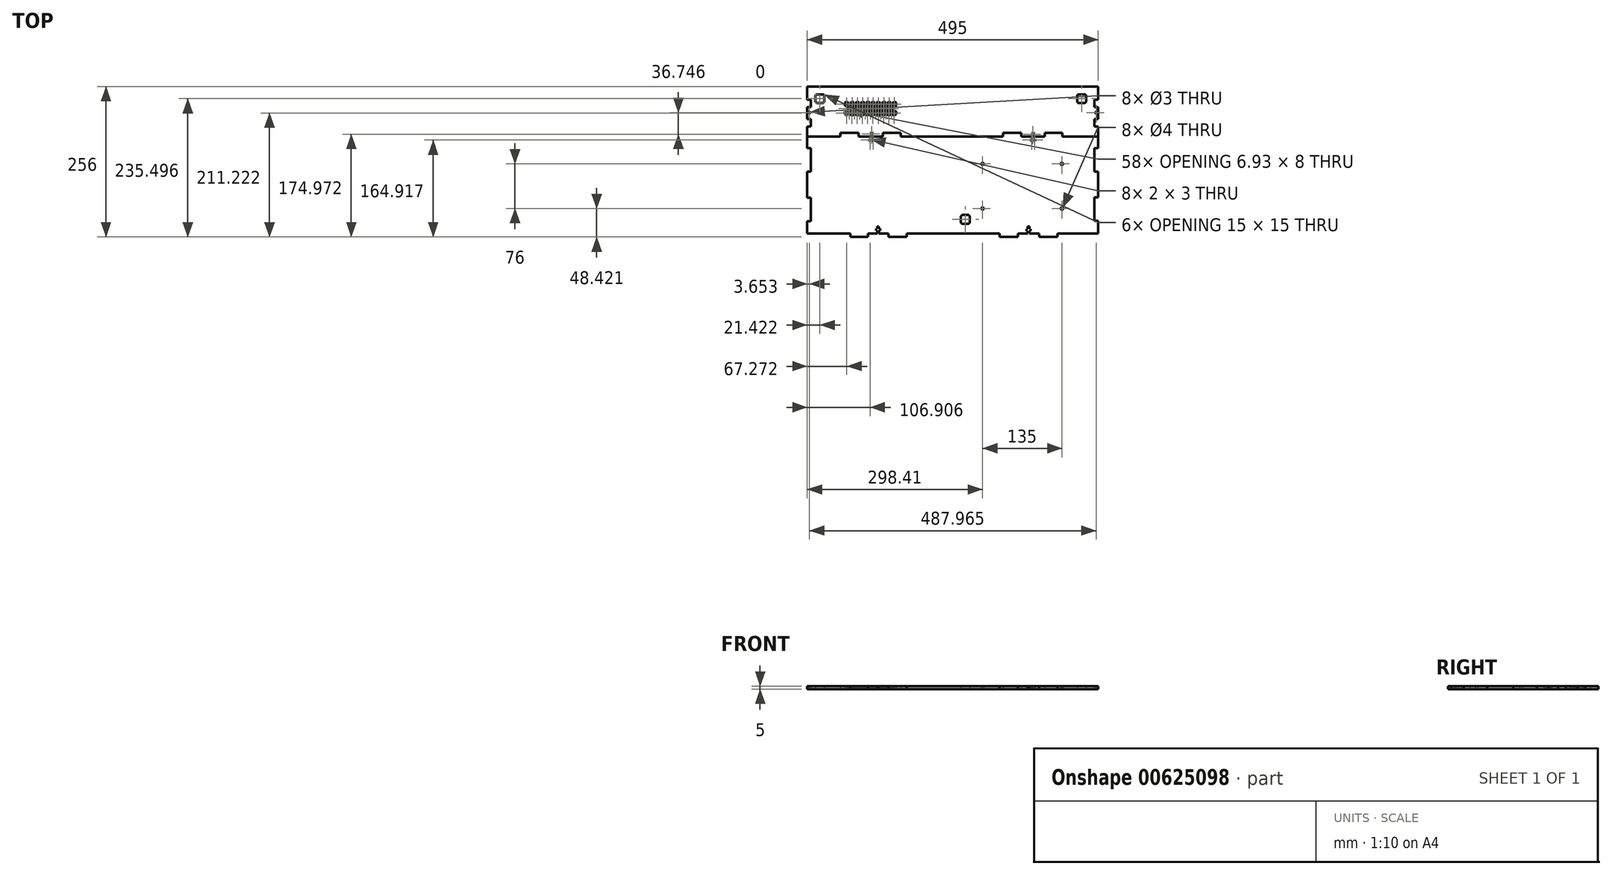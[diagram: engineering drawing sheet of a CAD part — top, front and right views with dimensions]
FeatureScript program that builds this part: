
annotation { "Feature Type Name" : "Feature", "Feature Type Description" : "" }
export const myFeature = defineFeature(function(context is Context, id is Id, definition is map)
    precondition{}
    {
        {
            var Q0;
            Q0=qCreatedBy(makeId("Top.planeOp"),FACE);
            var sketch = newSketch(context, id + "F0", { "sketchPlane" : qUnion([Q0])});
            skLineSegment(sketch, "E0", {"start": v(-326.42, 225.57) * mm, "end": v(-326.42, -168.8) * mm, "construction": true});
            skLineSegment(sketch, "E1", {"start": v(373.58, 224.27) * mm, "end": v(373.58, -247.98) * mm, "construction": true});
            skLineSegment(sketch, "E2.bottom", {"start": v(-274, -72) * mm, "end": v(221, -72) * mm});
            skLineSegment(sketch, "E2.top", {"start": v(-274, -237) * mm, "end": v(221, -237) * mm});
            skLineSegment(sketch, "E2.left", {"start": v(-274, -72) * mm, "end": v(-274, -237) * mm});
            skLineSegment(sketch, "E2.right", {"start": v(221, -72) * mm, "end": v(221, -237) * mm});
            skLineSegment(sketch, "E3", {"start": v(-200.57, -237) * mm, "end": v(-200.57, -243) * mm});
            skLineSegment(sketch, "E4", {"start": v(-200.57, -243) * mm, "end": v(-170.57, -243) * mm});
            skLineSegment(sketch, "E5", {"start": v(-170.57, -243) * mm, "end": v(-170.57, -237) * mm});
            skLineSegment(sketch, "E6", {"start": v(-135.94, -237) * mm, "end": v(-135.94, -243) * mm});
            skLineSegment(sketch, "E7", {"start": v(-135.94, -243) * mm, "end": v(-104.94, -243) * mm});
            skLineSegment(sketch, "E8", {"start": v(-104.94, -243) * mm, "end": v(-104.94, -237) * mm});
            skLineSegment(sketch, "E9", {"start": v(-186.48, -72) * mm, "end": v(-186.48, -66) * mm});
            skLineSegment(sketch, "E10", {"start": v(-186.48, -66) * mm, "end": v(-217.48, -66) * mm});
            skLineSegment(sketch, "E11", {"start": v(-217.48, -66) * mm, "end": v(-217.48, -72) * mm});
            skLineSegment(sketch, "E12", {"start": v(-114.63, -72) * mm, "end": v(-114.63, -66) * mm});
            skLineSegment(sketch, "E13", {"start": v(-114.63, -66) * mm, "end": v(-145.63, -66) * mm});
            skLineSegment(sketch, "E14", {"start": v(-145.63, -66) * mm, "end": v(-145.63, -72) * mm});
            skLineSegment(sketch, "E15", {"start": v(90.27, -72) * mm, "end": v(90.27, -66) * mm});
            skLineSegment(sketch, "E16", {"start": v(90.27, -66) * mm, "end": v(59.27, -66) * mm});
            skLineSegment(sketch, "E17", {"start": v(59.27, -66) * mm, "end": v(59.27, -72) * mm});
            skLineSegment(sketch, "E18", {"start": v(130.37, -72) * mm, "end": v(130.37, -66) * mm});
            skLineSegment(sketch, "E19", {"start": v(130.37, -66) * mm, "end": v(160.37, -66) * mm});
            skLineSegment(sketch, "E20", {"start": v(160.37, -66) * mm, "end": v(160.37, -72) * mm});
            skLineSegment(sketch, "E21", {"start": v(221, -91.47) * mm, "end": v(215, -91.47) * mm});
            skLineSegment(sketch, "E22", {"start": v(215, -91.47) * mm, "end": v(215, -131.47) * mm});
            skLineSegment(sketch, "E23", {"start": v(215, -131.47) * mm, "end": v(221, -131.47) * mm});
            skLineSegment(sketch, "E24", {"start": v(221, -175.85) * mm, "end": v(215, -175.85) * mm});
            skLineSegment(sketch, "E25", {"start": v(215, -175.85) * mm, "end": v(215, -215.85) * mm});
            skLineSegment(sketch, "E26", {"start": v(215, -215.85) * mm, "end": v(221, -215.85) * mm});
            skLineSegment(sketch, "E27", {"start": v(151.6, -237) * mm, "end": v(151.6, -243) * mm});
            skLineSegment(sketch, "E28", {"start": v(151.6, -243) * mm, "end": v(120.6, -243) * mm});
            skLineSegment(sketch, "E29", {"start": v(120.6, -243) * mm, "end": v(120.6, -237) * mm});
            skLineSegment(sketch, "E30", {"start": v(84.66, -237) * mm, "end": v(84.66, -243) * mm});
            skLineSegment(sketch, "E31", {"start": v(84.66, -243) * mm, "end": v(53.66, -243) * mm});
            skLineSegment(sketch, "E32", {"start": v(53.66, -243) * mm, "end": v(53.66, -237) * mm});
            skLineSegment(sketch, "E33", {"start": v(-274, -91.57) * mm, "end": v(-268, -91.57) * mm});
            skLineSegment(sketch, "E34", {"start": v(-268, -91.57) * mm, "end": v(-268, -131.57) * mm});
            skLineSegment(sketch, "E35", {"start": v(-268, -131.57) * mm, "end": v(-274, -131.57) * mm});
            skLineSegment(sketch, "E36", {"start": v(-274, -176.4) * mm, "end": v(-268, -176.4) * mm});
            skLineSegment(sketch, "E37", {"start": v(-268, -176.4) * mm, "end": v(-268, -216.4) * mm});
            skLineSegment(sketch, "E38", {"start": v(-268, -216.4) * mm, "end": v(-274, -216.4) * mm});
            skLineSegment(sketch, "E39", {"start": v(-155.1, -237) * mm, "end": v(-155.1, -225) * mm});
            skLineSegment(sketch, "E40", {"start": v(-155.1, -225) * mm, "end": v(-152.1, -225) * mm});
            skLineSegment(sketch, "E41", {"start": v(-152.1, -225) * mm, "end": v(-152.1, -237) * mm});
            skLineSegment(sketch, "E42", {"start": v(-155.1, -229) * mm, "end": v(-157.1, -229) * mm});
            skLineSegment(sketch, "E43", {"start": v(-157.1, -229) * mm, "end": v(-157.1, -232) * mm});
            skLineSegment(sketch, "E44", {"start": v(-157.1, -232) * mm, "end": v(-155.1, -232) * mm});
            skLineSegment(sketch, "E45", {"start": v(-152.1, -229) * mm, "end": v(-150.1, -229) * mm});
            skLineSegment(sketch, "E46", {"start": v(-150.1, -229) * mm, "end": v(-150.1, -232) * mm});
            skLineSegment(sketch, "E47", {"start": v(-150.1, -232) * mm, "end": v(-152.1, -232) * mm});
            skLineSegment(sketch, "E48", {"start": v(-308.95, -154.5) * mm, "end": v(259.37, -154.5) * mm, "construction": true});
            skLineSegment(sketch, "E49", {"start": v(-155.1, -237) * mm, "end": v(-152.1, -237) * mm});
            skLineSegment(sketch, "E50.1.0.0", {"start": v(100.9, -237) * mm, "end": v(103.9, -237) * mm});
            skLineSegment(sketch, "E50.1.0.1", {"start": v(100.9, -237) * mm, "end": v(100.9, -225) * mm});
            skLineSegment(sketch, "E50.1.0.2", {"start": v(98.9, -232.57) * mm, "end": v(100.9, -232.57) * mm});
            skLineSegment(sketch, "E50.1.0.3", {"start": v(98.9, -229.57) * mm, "end": v(98.9, -232.57) * mm});
            skLineSegment(sketch, "E50.1.0.4", {"start": v(100.9, -229.57) * mm, "end": v(98.9, -229.57) * mm});
            skLineSegment(sketch, "E50.1.0.5", {"start": v(100.9, -225) * mm, "end": v(103.9, -225) * mm});
            skLineSegment(sketch, "E50.1.0.6", {"start": v(103.9, -225) * mm, "end": v(103.9, -237) * mm});
            skLineSegment(sketch, "E50.1.0.7", {"start": v(103.9, -229.57) * mm, "end": v(105.9, -229.57) * mm});
            skLineSegment(sketch, "E50.1.0.8", {"start": v(105.9, -232.57) * mm, "end": v(103.9, -232.57) * mm});
            skLineSegment(sketch, "E50.1.0.9", {"start": v(105.9, -229.57) * mm, "end": v(105.9, -232.57) * mm});
            skLineSegment(sketch, "E50.direction1", {"start": v(-155.1, -237) * mm, "end": v(100.9, -237) * mm, "construction": true});
            skLineSegment(sketch, "E51.MirrorCS", {"start": v(108.9, -84.07) * mm, "end": v(111.9, -84.07) * mm});
            skLineSegment(sketch, "E52.MirrorCS", {"start": v(111.9, -79.57) * mm, "end": v(113.9, -79.57) * mm});
            skLineSegment(sketch, "E53.MirrorCS", {"start": v(113.9, -79.57) * mm, "end": v(113.9, -76.57) * mm});
            skLineSegment(sketch, "E54.MirrorCS", {"start": v(113.9, -76.57) * mm, "end": v(111.9, -76.57) * mm});
            skLineSegment(sketch, "E55.MirrorCS", {"start": v(111.9, -84.07) * mm, "end": v(111.9, -72.07) * mm});
            skLineSegment(sketch, "E56.MirrorCS", {"start": v(108.9, -79.57) * mm, "end": v(106.9, -79.57) * mm});
            skLineSegment(sketch, "E57.MirrorCS", {"start": v(106.9, -79.57) * mm, "end": v(106.9, -76.57) * mm});
            skLineSegment(sketch, "E58.MirrorCS", {"start": v(106.9, -76.57) * mm, "end": v(108.9, -76.57) * mm});
            skLineSegment(sketch, "E59.MirrorCS", {"start": v(108.9, -72.07) * mm, "end": v(108.9, -84.07) * mm});
            skLineSegment(sketch, "E60.MirrorCS", {"start": v(-166.1, -84.07) * mm, "end": v(-163.1, -84.07) * mm});
            skLineSegment(sketch, "E61.MirrorCS", {"start": v(-161.1, -79.57) * mm, "end": v(-161.1, -76.57) * mm});
            skLineSegment(sketch, "E62.MirrorCS", {"start": v(-163.1, -79.57) * mm, "end": v(-161.1, -79.57) * mm});
            skLineSegment(sketch, "E63.MirrorCS", {"start": v(-163.1, -84.07) * mm, "end": v(-163.1, -72.07) * mm});
            skLineSegment(sketch, "E64.MirrorCS", {"start": v(-161.1, -76.57) * mm, "end": v(-163.1, -76.57) * mm});
            skLineSegment(sketch, "E65.MirrorCS", {"start": v(-168.1, -76.57) * mm, "end": v(-166.1, -76.57) * mm});
            skLineSegment(sketch, "E66.MirrorCS", {"start": v(-168.1, -79.57) * mm, "end": v(-168.1, -76.57) * mm});
            skLineSegment(sketch, "E67.MirrorCS", {"start": v(-166.1, -72.07) * mm, "end": v(-166.1, -84.07) * mm});
            skLineSegment(sketch, "E68.MirrorCS", {"start": v(-166.1, -79.57) * mm, "end": v(-168.1, -79.57) * mm});
            skLineSegment(sketch, "E69.MirrorCS", {"start": v(100.9, -237.07) * mm, "end": v(100.9, -225.07) * mm});
            skLineSegment(sketch, "E70.bottom", {"start": v(-9.44, -205.6) * mm, "end": v(-0.44, -205.6) * mm});
            skLineSegment(sketch, "E70.top", {"start": v(-9.44, -220.6) * mm, "end": v(-0.44, -220.6) * mm});
            skLineSegment(sketch, "E70.left", {"start": v(-12.44, -208.6) * mm, "end": v(-12.44, -217.6) * mm});
            skLineSegment(sketch, "E70.right", {"start": v(2.56, -208.6) * mm, "end": v(2.56, -217.6) * mm});
            skPoint(sketch, "E71.visualSharp", {"position": v(-12.44, -205.6) * mm});
            skArc(sketch, "E71.filletArc", {"start": v(-9.44, -205.6) * mm, "mid": v(-11.56, -206.48) * mm, "end": v(-12.44, -208.6) * mm});
            skPoint(sketch, "E72.visualSharp", {"position": v(2.56, -205.6) * mm});
            skArc(sketch, "E72.filletArc", {"start": v(2.56, -208.6) * mm, "mid": v(1.69, -206.48) * mm, "end": v(-0.44, -205.6) * mm});
            skPoint(sketch, "E73.visualSharp", {"position": v(2.56, -220.6) * mm});
            skArc(sketch, "E73.filletArc", {"start": v(-0.44, -220.6) * mm, "mid": v(1.69, -219.73) * mm, "end": v(2.56, -217.6) * mm});
            skPoint(sketch, "E74.visualSharp", {"position": v(-12.44, -220.6) * mm});
            skArc(sketch, "E74.filletArc", {"start": v(-12.44, -217.6) * mm, "mid": v(-11.56, -219.73) * mm, "end": v(-9.44, -220.6) * mm});
            skCircle(sketch, "E75", {"center": v(24.41, -194.57) * mm, "radius": 2 * mm});
            skCircle(sketch, "E76.0.1.0", {"center": v(24.41, -118.57) * mm, "radius": 2 * mm});
            skCircle(sketch, "E76.1.0.0", {"center": v(159.41, -194.57) * mm, "radius": 2 * mm});
            skCircle(sketch, "E76.1.1.0", {"center": v(159.41, -118.57) * mm, "radius": 2 * mm});
            skLineSegment(sketch, "E76.direction1", {"start": v(24.41, -194.57) * mm, "end": v(159.41, -194.57) * mm, "construction": true});
            skLineSegment(sketch, "E76.direction2", {"start": v(24.41, -194.57) * mm, "end": v(24.41, -118.57) * mm, "construction": true});
            skLineSegment(sketch, "E77", {"start": v(-274, -72) * mm, "end": v(-274, 13) * mm});
            skLineSegment(sketch, "E78", {"start": v(-274, 13) * mm, "end": v(221, 13) * mm});
            skLineSegment(sketch, "E79", {"start": v(221, 13) * mm, "end": v(221, -72) * mm});
            skLineSegment(sketch, "E80", {"start": v(-274, -9.1) * mm, "end": v(-268, -9.1) * mm});
            skLineSegment(sketch, "E81", {"start": v(-268, -9.1) * mm, "end": v(-268, -22.1) * mm});
            skLineSegment(sketch, "E82", {"start": v(-268, -22.1) * mm, "end": v(-274, -22.1) * mm});
            skLineSegment(sketch, "E83", {"start": v(-274, -42.1) * mm, "end": v(-268, -42.1) * mm});
            skLineSegment(sketch, "E84", {"start": v(-268, -42.1) * mm, "end": v(-268, -55.1) * mm});
            skLineSegment(sketch, "E85", {"start": v(-268, -55.1) * mm, "end": v(-274, -55.1) * mm});
            skLineSegment(sketch, "E86", {"start": v(221, -9.1) * mm, "end": v(215, -9.1) * mm});
            skLineSegment(sketch, "E87", {"start": v(215, -9.1) * mm, "end": v(215, -22.1) * mm});
            skLineSegment(sketch, "E88", {"start": v(215, -22.1) * mm, "end": v(221, -22.1) * mm});
            skLineSegment(sketch, "E89", {"start": v(221, -42.1) * mm, "end": v(215, -42.1) * mm});
            skLineSegment(sketch, "E90", {"start": v(215, -42.1) * mm, "end": v(215, -55.1) * mm});
            skLineSegment(sketch, "E91", {"start": v(215, -55.1) * mm, "end": v(221, -55.1) * mm});
            skCircle(sketch, "E92", {"center": v(217.62, -31.36) * mm, "radius": 1.5 * mm});
            skCircle(sketch, "E93", {"center": v(-270.35, -31.27) * mm, "radius": 1.5 * mm});
            skLineSegment(sketch, "E94.bottom", {"start": v(-257.08, 0) * mm, "end": v(-248.08, 0) * mm});
            skLineSegment(sketch, "E94.top", {"start": v(-257.08, -15) * mm, "end": v(-248.08, -15) * mm});
            skLineSegment(sketch, "E94.left", {"start": v(-260.08, -3) * mm, "end": v(-260.08, -12) * mm});
            skLineSegment(sketch, "E94.right", {"start": v(-245.08, -3) * mm, "end": v(-245.08, -12) * mm});
            skPoint(sketch, "E95.visualSharp", {"position": v(-260.08, 0) * mm});
            skArc(sketch, "E95.filletArc", {"start": v(-257.08, 0) * mm, "mid": v(-259.2, -0.87) * mm, "end": v(-260.08, -3) * mm});
            skPoint(sketch, "E96.visualSharp", {"position": v(-245.08, 0) * mm});
            skArc(sketch, "E96.filletArc", {"start": v(-245.08, -3) * mm, "mid": v(-245.96, -0.87) * mm, "end": v(-248.08, 0) * mm});
            skPoint(sketch, "E97.visualSharp", {"position": v(-260.08, -15) * mm});
            skArc(sketch, "E97.filletArc", {"start": v(-260.08, -12) * mm, "mid": v(-259.2, -14.12) * mm, "end": v(-257.08, -15) * mm});
            skPoint(sketch, "E98.visualSharp", {"position": v(-245.08, -15) * mm});
            skArc(sketch, "E98.filletArc", {"start": v(-248.08, -15) * mm, "mid": v(-245.96, -14.12) * mm, "end": v(-245.08, -12) * mm});
            skLineSegment(sketch, "E99.bottom", {"start": v(188.51, 0) * mm, "end": v(197.51, 0) * mm});
            skLineSegment(sketch, "E99.top", {"start": v(188.51, -15) * mm, "end": v(197.51, -15) * mm});
            skLineSegment(sketch, "E99.left", {"start": v(185.51, -3) * mm, "end": v(185.51, -12) * mm});
            skLineSegment(sketch, "E99.right", {"start": v(200.51, -3) * mm, "end": v(200.51, -12) * mm});
            skPoint(sketch, "E100.visualSharp", {"position": v(185.51, 0) * mm});
            skArc(sketch, "E100.filletArc", {"start": v(188.51, 0) * mm, "mid": v(186.4, -0.87) * mm, "end": v(185.51, -3) * mm});
            skPoint(sketch, "E101.visualSharp", {"position": v(200.51, 0) * mm});
            skArc(sketch, "E101.filletArc", {"start": v(200.51, -3) * mm, "mid": v(199.63, -0.87) * mm, "end": v(197.51, 0) * mm});
            skPoint(sketch, "E102.visualSharp", {"position": v(185.51, -15) * mm});
            skArc(sketch, "E102.filletArc", {"start": v(185.51, -12) * mm, "mid": v(186.4, -14.12) * mm, "end": v(188.51, -15) * mm});
            skPoint(sketch, "E103.visualSharp", {"position": v(200.51, -15) * mm});
            skArc(sketch, "E103.filletArc", {"start": v(197.51, -15) * mm, "mid": v(199.63, -14.12) * mm, "end": v(200.51, -12) * mm});
            skCircle(sketch, "E104", {"center": v(-164.6, -67.51) * mm, "radius": 1.5 * mm});
            skCircle(sketch, "E105", {"center": v(110, -68.02) * mm, "radius": 1.5 * mm});
            skCircle(sketch, "E106.cCircle", {"center": v(-206.73, -17.03) * mm, "radius": 4 * mm, "construction": true});
            skLineSegment(sketch, "E106.0", {"start": v(-203.26, -15.03) * mm, "end": v(-203.26, -19.03) * mm});
            skLineSegment(sketch, "E106.1", {"start": v(-203.26, -19.03) * mm, "end": v(-206.73, -21.03) * mm});
            skLineSegment(sketch, "E106.2", {"start": v(-206.73, -21.03) * mm, "end": v(-210.2, -19.03) * mm});
            skLineSegment(sketch, "E106.3", {"start": v(-210.2, -19.03) * mm, "end": v(-210.2, -15.03) * mm});
            skLineSegment(sketch, "E106.4", {"start": v(-210.2, -15.03) * mm, "end": v(-206.73, -13.03) * mm});
            skLineSegment(sketch, "E106.5", {"start": v(-206.73, -13.03) * mm, "end": v(-203.26, -15.03) * mm});
            skLineSegment(sketch, "E107.0.1.0", {"start": v(-205.94, -26.4) * mm, "end": v(-205.94, -22.4) * mm});
            skLineSegment(sketch, "E107.0.1.1", {"start": v(-205.94, -22.4) * mm, "end": v(-202.47, -20.4) * mm});
            skLineSegment(sketch, "E107.0.1.2", {"start": v(-202.47, -20.4) * mm, "end": v(-199, -22.4) * mm});
            skLineSegment(sketch, "E107.0.1.3", {"start": v(-199, -22.4) * mm, "end": v(-199, -26.4) * mm});
            skLineSegment(sketch, "E107.0.1.4", {"start": v(-199, -26.4) * mm, "end": v(-202.47, -28.4) * mm});
            skLineSegment(sketch, "E107.0.1.5", {"start": v(-202.47, -28.4) * mm, "end": v(-205.94, -26.4) * mm});
            skLineSegment(sketch, "E107.0.2.0", {"start": v(-201.68, -33.77) * mm, "end": v(-201.68, -29.77) * mm});
            skLineSegment(sketch, "E107.0.2.1", {"start": v(-201.68, -29.77) * mm, "end": v(-198.22, -27.77) * mm});
            skLineSegment(sketch, "E107.0.2.2", {"start": v(-198.22, -27.77) * mm, "end": v(-194.75, -29.77) * mm});
            skLineSegment(sketch, "E107.0.2.3", {"start": v(-194.75, -29.77) * mm, "end": v(-194.75, -33.77) * mm});
            skLineSegment(sketch, "E107.0.2.4", {"start": v(-194.75, -33.77) * mm, "end": v(-198.22, -35.77) * mm});
            skLineSegment(sketch, "E107.0.2.5", {"start": v(-198.22, -35.77) * mm, "end": v(-201.68, -33.77) * mm});
            skLineSegment(sketch, "E107.1.0.0", {"start": v(-201.2, -19.03) * mm, "end": v(-201.2, -15.03) * mm});
            skLineSegment(sketch, "E107.1.0.1", {"start": v(-201.2, -15.03) * mm, "end": v(-197.73, -13.03) * mm});
            skLineSegment(sketch, "E107.1.0.2", {"start": v(-197.73, -13.03) * mm, "end": v(-194.26, -15.03) * mm});
            skLineSegment(sketch, "E107.1.0.3", {"start": v(-194.26, -15.03) * mm, "end": v(-194.26, -19.03) * mm});
            skLineSegment(sketch, "E107.1.0.4", {"start": v(-194.26, -19.03) * mm, "end": v(-197.73, -21.03) * mm});
            skLineSegment(sketch, "E107.1.0.5", {"start": v(-197.73, -21.03) * mm, "end": v(-201.2, -19.03) * mm});
            skLineSegment(sketch, "E107.1.1.0", {"start": v(-196.94, -26.4) * mm, "end": v(-196.94, -22.4) * mm});
            skLineSegment(sketch, "E107.1.1.1", {"start": v(-196.94, -22.4) * mm, "end": v(-193.47, -20.4) * mm});
            skLineSegment(sketch, "E107.1.1.2", {"start": v(-193.47, -20.4) * mm, "end": v(-190, -22.4) * mm});
            skLineSegment(sketch, "E107.1.1.3", {"start": v(-190, -22.4) * mm, "end": v(-190, -26.4) * mm});
            skLineSegment(sketch, "E107.1.1.4", {"start": v(-190, -26.4) * mm, "end": v(-193.47, -28.4) * mm});
            skLineSegment(sketch, "E107.1.1.5", {"start": v(-193.47, -28.4) * mm, "end": v(-196.94, -26.4) * mm});
            skLineSegment(sketch, "E107.1.2.0", {"start": v(-192.68, -33.77) * mm, "end": v(-192.68, -29.77) * mm});
            skLineSegment(sketch, "E107.1.2.1", {"start": v(-192.68, -29.77) * mm, "end": v(-189.22, -27.77) * mm});
            skLineSegment(sketch, "E107.1.2.2", {"start": v(-189.22, -27.77) * mm, "end": v(-185.75, -29.77) * mm});
            skLineSegment(sketch, "E107.1.2.3", {"start": v(-185.75, -29.77) * mm, "end": v(-185.75, -33.77) * mm});
            skLineSegment(sketch, "E107.1.2.4", {"start": v(-185.75, -33.77) * mm, "end": v(-189.22, -35.77) * mm});
            skLineSegment(sketch, "E107.1.2.5", {"start": v(-189.22, -35.77) * mm, "end": v(-192.68, -33.77) * mm});
            skLineSegment(sketch, "E107.2.0.0", {"start": v(-192.2, -19.03) * mm, "end": v(-192.2, -15.03) * mm});
            skLineSegment(sketch, "E107.2.0.1", {"start": v(-192.2, -15.03) * mm, "end": v(-188.73, -13.03) * mm});
            skLineSegment(sketch, "E107.2.0.2", {"start": v(-188.73, -13.03) * mm, "end": v(-185.26, -15.03) * mm});
            skLineSegment(sketch, "E107.2.0.3", {"start": v(-185.26, -15.03) * mm, "end": v(-185.26, -19.03) * mm});
            skLineSegment(sketch, "E107.2.0.4", {"start": v(-185.26, -19.03) * mm, "end": v(-188.73, -21.03) * mm});
            skLineSegment(sketch, "E107.2.0.5", {"start": v(-188.73, -21.03) * mm, "end": v(-192.2, -19.03) * mm});
            skLineSegment(sketch, "E107.2.1.0", {"start": v(-187.94, -26.4) * mm, "end": v(-187.94, -22.4) * mm});
            skLineSegment(sketch, "E107.2.1.1", {"start": v(-187.94, -22.4) * mm, "end": v(-184.47, -20.4) * mm});
            skLineSegment(sketch, "E107.2.1.2", {"start": v(-184.47, -20.4) * mm, "end": v(-181, -22.4) * mm});
            skLineSegment(sketch, "E107.2.1.3", {"start": v(-181, -22.4) * mm, "end": v(-181, -26.4) * mm});
            skLineSegment(sketch, "E107.2.1.4", {"start": v(-181, -26.4) * mm, "end": v(-184.47, -28.4) * mm});
            skLineSegment(sketch, "E107.2.1.5", {"start": v(-184.47, -28.4) * mm, "end": v(-187.94, -26.4) * mm});
            skLineSegment(sketch, "E107.2.2.0", {"start": v(-183.68, -33.77) * mm, "end": v(-183.68, -29.77) * mm});
            skLineSegment(sketch, "E107.2.2.1", {"start": v(-183.68, -29.77) * mm, "end": v(-180.22, -27.77) * mm});
            skLineSegment(sketch, "E107.2.2.2", {"start": v(-180.22, -27.77) * mm, "end": v(-176.75, -29.77) * mm});
            skLineSegment(sketch, "E107.2.2.3", {"start": v(-176.75, -29.77) * mm, "end": v(-176.75, -33.77) * mm});
            skLineSegment(sketch, "E107.2.2.4", {"start": v(-176.75, -33.77) * mm, "end": v(-180.22, -35.77) * mm});
            skLineSegment(sketch, "E107.2.2.5", {"start": v(-180.22, -35.77) * mm, "end": v(-183.68, -33.77) * mm});
            skLineSegment(sketch, "E107.3.0.0", {"start": v(-183.2, -19.03) * mm, "end": v(-183.2, -15.03) * mm});
            skLineSegment(sketch, "E107.3.0.1", {"start": v(-183.2, -15.03) * mm, "end": v(-179.73, -13.03) * mm});
            skLineSegment(sketch, "E107.3.0.2", {"start": v(-179.73, -13.03) * mm, "end": v(-176.26, -15.03) * mm});
            skLineSegment(sketch, "E107.3.0.3", {"start": v(-176.26, -15.03) * mm, "end": v(-176.26, -19.03) * mm});
            skLineSegment(sketch, "E107.3.0.4", {"start": v(-176.26, -19.03) * mm, "end": v(-179.73, -21.03) * mm});
            skLineSegment(sketch, "E107.3.0.5", {"start": v(-179.73, -21.03) * mm, "end": v(-183.2, -19.03) * mm});
            skLineSegment(sketch, "E107.3.1.0", {"start": v(-178.94, -26.4) * mm, "end": v(-178.94, -22.4) * mm});
            skLineSegment(sketch, "E107.3.1.1", {"start": v(-178.94, -22.4) * mm, "end": v(-175.47, -20.4) * mm});
            skLineSegment(sketch, "E107.3.1.2", {"start": v(-175.47, -20.4) * mm, "end": v(-172, -22.4) * mm});
            skLineSegment(sketch, "E107.3.1.3", {"start": v(-172, -22.4) * mm, "end": v(-172, -26.4) * mm});
            skLineSegment(sketch, "E107.3.1.4", {"start": v(-172, -26.4) * mm, "end": v(-175.47, -28.4) * mm});
            skLineSegment(sketch, "E107.3.1.5", {"start": v(-175.47, -28.4) * mm, "end": v(-178.94, -26.4) * mm});
            skLineSegment(sketch, "E107.3.2.0", {"start": v(-174.68, -33.77) * mm, "end": v(-174.68, -29.77) * mm});
            skLineSegment(sketch, "E107.3.2.1", {"start": v(-174.68, -29.77) * mm, "end": v(-171.22, -27.77) * mm});
            skLineSegment(sketch, "E107.3.2.2", {"start": v(-171.22, -27.77) * mm, "end": v(-167.75, -29.77) * mm});
            skLineSegment(sketch, "E107.3.2.3", {"start": v(-167.75, -29.77) * mm, "end": v(-167.75, -33.77) * mm});
            skLineSegment(sketch, "E107.3.2.4", {"start": v(-167.75, -33.77) * mm, "end": v(-171.22, -35.77) * mm});
            skLineSegment(sketch, "E107.3.2.5", {"start": v(-171.22, -35.77) * mm, "end": v(-174.68, -33.77) * mm});
            skLineSegment(sketch, "E107.4.0.0", {"start": v(-174.2, -19.03) * mm, "end": v(-174.2, -15.03) * mm});
            skLineSegment(sketch, "E107.4.0.1", {"start": v(-174.2, -15.03) * mm, "end": v(-170.73, -13.03) * mm});
            skLineSegment(sketch, "E107.4.0.2", {"start": v(-170.73, -13.03) * mm, "end": v(-167.26, -15.03) * mm});
            skLineSegment(sketch, "E107.4.0.3", {"start": v(-167.26, -15.03) * mm, "end": v(-167.26, -19.03) * mm});
            skLineSegment(sketch, "E107.4.0.4", {"start": v(-167.26, -19.03) * mm, "end": v(-170.73, -21.03) * mm});
            skLineSegment(sketch, "E107.4.0.5", {"start": v(-170.73, -21.03) * mm, "end": v(-174.2, -19.03) * mm});
            skLineSegment(sketch, "E107.4.1.0", {"start": v(-169.94, -26.4) * mm, "end": v(-169.94, -22.4) * mm});
            skLineSegment(sketch, "E107.4.1.1", {"start": v(-169.94, -22.4) * mm, "end": v(-166.47, -20.4) * mm});
            skLineSegment(sketch, "E107.4.1.2", {"start": v(-166.47, -20.4) * mm, "end": v(-163, -22.4) * mm});
            skLineSegment(sketch, "E107.4.1.3", {"start": v(-163, -22.4) * mm, "end": v(-163, -26.4) * mm});
            skLineSegment(sketch, "E107.4.1.4", {"start": v(-163, -26.4) * mm, "end": v(-166.47, -28.4) * mm});
            skLineSegment(sketch, "E107.4.1.5", {"start": v(-166.47, -28.4) * mm, "end": v(-169.94, -26.4) * mm});
            skLineSegment(sketch, "E107.4.2.0", {"start": v(-165.68, -33.77) * mm, "end": v(-165.68, -29.77) * mm});
            skLineSegment(sketch, "E107.4.2.1", {"start": v(-165.68, -29.77) * mm, "end": v(-162.22, -27.77) * mm});
            skLineSegment(sketch, "E107.4.2.2", {"start": v(-162.22, -27.77) * mm, "end": v(-158.75, -29.77) * mm});
            skLineSegment(sketch, "E107.4.2.3", {"start": v(-158.75, -29.77) * mm, "end": v(-158.75, -33.77) * mm});
            skLineSegment(sketch, "E107.4.2.4", {"start": v(-158.75, -33.77) * mm, "end": v(-162.22, -35.77) * mm});
            skLineSegment(sketch, "E107.4.2.5", {"start": v(-162.22, -35.77) * mm, "end": v(-165.68, -33.77) * mm});
            skLineSegment(sketch, "E107.5.0.0", {"start": v(-165.2, -19.03) * mm, "end": v(-165.2, -15.03) * mm});
            skLineSegment(sketch, "E107.5.0.1", {"start": v(-165.2, -15.03) * mm, "end": v(-161.73, -13.03) * mm});
            skLineSegment(sketch, "E107.5.0.2", {"start": v(-161.73, -13.03) * mm, "end": v(-158.26, -15.03) * mm});
            skLineSegment(sketch, "E107.5.0.3", {"start": v(-158.26, -15.03) * mm, "end": v(-158.26, -19.03) * mm});
            skLineSegment(sketch, "E107.5.0.4", {"start": v(-158.26, -19.03) * mm, "end": v(-161.73, -21.03) * mm});
            skLineSegment(sketch, "E107.5.0.5", {"start": v(-161.73, -21.03) * mm, "end": v(-165.2, -19.03) * mm});
            skLineSegment(sketch, "E107.5.1.0", {"start": v(-160.94, -26.4) * mm, "end": v(-160.94, -22.4) * mm});
            skLineSegment(sketch, "E107.5.1.1", {"start": v(-160.94, -22.4) * mm, "end": v(-157.47, -20.4) * mm});
            skLineSegment(sketch, "E107.5.1.2", {"start": v(-157.47, -20.4) * mm, "end": v(-154, -22.4) * mm});
            skLineSegment(sketch, "E107.5.1.3", {"start": v(-154, -22.4) * mm, "end": v(-154, -26.4) * mm});
            skLineSegment(sketch, "E107.5.1.4", {"start": v(-154, -26.4) * mm, "end": v(-157.47, -28.4) * mm});
            skLineSegment(sketch, "E107.5.1.5", {"start": v(-157.47, -28.4) * mm, "end": v(-160.94, -26.4) * mm});
            skLineSegment(sketch, "E107.5.2.0", {"start": v(-156.68, -33.77) * mm, "end": v(-156.68, -29.77) * mm});
            skLineSegment(sketch, "E107.5.2.1", {"start": v(-156.68, -29.77) * mm, "end": v(-153.22, -27.77) * mm});
            skLineSegment(sketch, "E107.5.2.2", {"start": v(-153.22, -27.77) * mm, "end": v(-149.75, -29.77) * mm});
            skLineSegment(sketch, "E107.5.2.3", {"start": v(-149.75, -29.77) * mm, "end": v(-149.75, -33.77) * mm});
            skLineSegment(sketch, "E107.5.2.4", {"start": v(-149.75, -33.77) * mm, "end": v(-153.22, -35.77) * mm});
            skLineSegment(sketch, "E107.5.2.5", {"start": v(-153.22, -35.77) * mm, "end": v(-156.68, -33.77) * mm});
            skLineSegment(sketch, "E107.6.0.0", {"start": v(-156.2, -19.03) * mm, "end": v(-156.2, -15.03) * mm});
            skLineSegment(sketch, "E107.6.0.1", {"start": v(-156.2, -15.03) * mm, "end": v(-152.73, -13.03) * mm});
            skLineSegment(sketch, "E107.6.0.2", {"start": v(-152.73, -13.03) * mm, "end": v(-149.26, -15.03) * mm});
            skLineSegment(sketch, "E107.6.0.3", {"start": v(-149.26, -15.03) * mm, "end": v(-149.26, -19.03) * mm});
            skLineSegment(sketch, "E107.6.0.4", {"start": v(-149.26, -19.03) * mm, "end": v(-152.73, -21.03) * mm});
            skLineSegment(sketch, "E107.6.0.5", {"start": v(-152.73, -21.03) * mm, "end": v(-156.2, -19.03) * mm});
            skLineSegment(sketch, "E107.6.1.0", {"start": v(-151.94, -26.4) * mm, "end": v(-151.94, -22.4) * mm});
            skLineSegment(sketch, "E107.6.1.1", {"start": v(-151.94, -22.4) * mm, "end": v(-148.47, -20.4) * mm});
            skLineSegment(sketch, "E107.6.1.2", {"start": v(-148.47, -20.4) * mm, "end": v(-145, -22.4) * mm});
            skLineSegment(sketch, "E107.6.1.3", {"start": v(-145, -22.4) * mm, "end": v(-145, -26.4) * mm});
            skLineSegment(sketch, "E107.6.1.4", {"start": v(-145, -26.4) * mm, "end": v(-148.47, -28.4) * mm});
            skLineSegment(sketch, "E107.6.1.5", {"start": v(-148.47, -28.4) * mm, "end": v(-151.94, -26.4) * mm});
            skLineSegment(sketch, "E107.6.2.0", {"start": v(-147.68, -33.77) * mm, "end": v(-147.68, -29.77) * mm});
            skLineSegment(sketch, "E107.6.2.1", {"start": v(-147.68, -29.77) * mm, "end": v(-144.22, -27.77) * mm});
            skLineSegment(sketch, "E107.6.2.2", {"start": v(-144.22, -27.77) * mm, "end": v(-140.75, -29.77) * mm});
            skLineSegment(sketch, "E107.6.2.3", {"start": v(-140.75, -29.77) * mm, "end": v(-140.75, -33.77) * mm});
            skLineSegment(sketch, "E107.6.2.4", {"start": v(-140.75, -33.77) * mm, "end": v(-144.22, -35.77) * mm});
            skLineSegment(sketch, "E107.6.2.5", {"start": v(-144.22, -35.77) * mm, "end": v(-147.68, -33.77) * mm});
            skLineSegment(sketch, "E107.7.0.0", {"start": v(-147.2, -19.03) * mm, "end": v(-147.2, -15.03) * mm});
            skLineSegment(sketch, "E107.7.0.1", {"start": v(-147.2, -15.03) * mm, "end": v(-143.73, -13.03) * mm});
            skLineSegment(sketch, "E107.7.0.2", {"start": v(-143.73, -13.03) * mm, "end": v(-140.26, -15.03) * mm});
            skLineSegment(sketch, "E107.7.0.3", {"start": v(-140.26, -15.03) * mm, "end": v(-140.26, -19.03) * mm});
            skLineSegment(sketch, "E107.7.0.4", {"start": v(-140.26, -19.03) * mm, "end": v(-143.73, -21.03) * mm});
            skLineSegment(sketch, "E107.7.0.5", {"start": v(-143.73, -21.03) * mm, "end": v(-147.2, -19.03) * mm});
            skLineSegment(sketch, "E107.7.1.0", {"start": v(-142.94, -26.4) * mm, "end": v(-142.94, -22.4) * mm});
            skLineSegment(sketch, "E107.7.1.1", {"start": v(-142.94, -22.4) * mm, "end": v(-139.47, -20.4) * mm});
            skLineSegment(sketch, "E107.7.1.2", {"start": v(-139.47, -20.4) * mm, "end": v(-136, -22.4) * mm});
            skLineSegment(sketch, "E107.7.1.3", {"start": v(-136, -22.4) * mm, "end": v(-136, -26.4) * mm});
            skLineSegment(sketch, "E107.7.1.4", {"start": v(-136, -26.4) * mm, "end": v(-139.47, -28.4) * mm});
            skLineSegment(sketch, "E107.7.1.5", {"start": v(-139.47, -28.4) * mm, "end": v(-142.94, -26.4) * mm});
            skLineSegment(sketch, "E107.7.2.0", {"start": v(-138.68, -33.77) * mm, "end": v(-138.68, -29.77) * mm});
            skLineSegment(sketch, "E107.7.2.1", {"start": v(-138.68, -29.77) * mm, "end": v(-135.22, -27.77) * mm});
            skLineSegment(sketch, "E107.7.2.2", {"start": v(-135.22, -27.77) * mm, "end": v(-131.75, -29.77) * mm});
            skLineSegment(sketch, "E107.7.2.3", {"start": v(-131.75, -29.77) * mm, "end": v(-131.75, -33.77) * mm});
            skLineSegment(sketch, "E107.7.2.4", {"start": v(-131.75, -33.77) * mm, "end": v(-135.22, -35.77) * mm});
            skLineSegment(sketch, "E107.7.2.5", {"start": v(-135.22, -35.77) * mm, "end": v(-138.68, -33.77) * mm});
            skLineSegment(sketch, "E107.8.0.0", {"start": v(-138.2, -19.03) * mm, "end": v(-138.2, -15.03) * mm});
            skLineSegment(sketch, "E107.8.0.1", {"start": v(-138.2, -15.03) * mm, "end": v(-134.73, -13.03) * mm});
            skLineSegment(sketch, "E107.8.0.2", {"start": v(-134.73, -13.03) * mm, "end": v(-131.26, -15.03) * mm});
            skLineSegment(sketch, "E107.8.0.3", {"start": v(-131.26, -15.03) * mm, "end": v(-131.26, -19.03) * mm});
            skLineSegment(sketch, "E107.8.0.4", {"start": v(-131.26, -19.03) * mm, "end": v(-134.73, -21.03) * mm});
            skLineSegment(sketch, "E107.8.0.5", {"start": v(-134.73, -21.03) * mm, "end": v(-138.2, -19.03) * mm});
            skLineSegment(sketch, "E107.8.1.0", {"start": v(-133.94, -26.4) * mm, "end": v(-133.94, -22.4) * mm});
            skLineSegment(sketch, "E107.8.1.1", {"start": v(-133.94, -22.4) * mm, "end": v(-130.47, -20.4) * mm});
            skLineSegment(sketch, "E107.8.1.2", {"start": v(-130.47, -20.4) * mm, "end": v(-127, -22.4) * mm});
            skLineSegment(sketch, "E107.8.1.3", {"start": v(-127, -22.4) * mm, "end": v(-127, -26.4) * mm});
            skLineSegment(sketch, "E107.8.1.4", {"start": v(-127, -26.4) * mm, "end": v(-130.47, -28.4) * mm});
            skLineSegment(sketch, "E107.8.1.5", {"start": v(-130.47, -28.4) * mm, "end": v(-133.94, -26.4) * mm});
            skLineSegment(sketch, "E107.8.2.0", {"start": v(-129.68, -33.77) * mm, "end": v(-129.68, -29.77) * mm});
            skLineSegment(sketch, "E107.8.2.1", {"start": v(-129.68, -29.77) * mm, "end": v(-126.22, -27.77) * mm});
            skLineSegment(sketch, "E107.8.2.2", {"start": v(-126.22, -27.77) * mm, "end": v(-122.75, -29.77) * mm});
            skLineSegment(sketch, "E107.8.2.3", {"start": v(-122.75, -29.77) * mm, "end": v(-122.75, -33.77) * mm});
            skLineSegment(sketch, "E107.8.2.4", {"start": v(-122.75, -33.77) * mm, "end": v(-126.22, -35.77) * mm});
            skLineSegment(sketch, "E107.8.2.5", {"start": v(-126.22, -35.77) * mm, "end": v(-129.68, -33.77) * mm});
            skLineSegment(sketch, "E107.9.0.0", {"start": v(-129.2, -19.03) * mm, "end": v(-129.2, -15.03) * mm});
            skLineSegment(sketch, "E107.9.0.1", {"start": v(-129.2, -15.03) * mm, "end": v(-125.73, -13.03) * mm});
            skLineSegment(sketch, "E107.9.0.2", {"start": v(-125.73, -13.03) * mm, "end": v(-122.26, -15.03) * mm});
            skLineSegment(sketch, "E107.9.0.3", {"start": v(-122.26, -15.03) * mm, "end": v(-122.26, -19.03) * mm});
            skLineSegment(sketch, "E107.9.0.4", {"start": v(-122.26, -19.03) * mm, "end": v(-125.73, -21.03) * mm});
            skLineSegment(sketch, "E107.9.0.5", {"start": v(-125.73, -21.03) * mm, "end": v(-129.2, -19.03) * mm});
            skLineSegment(sketch, "E107.9.2.0", {"start": v(-210.2, -33.77) * mm, "end": v(-210.2, -29.77) * mm});
            skLineSegment(sketch, "E107.9.2.1", {"start": v(-210.2, -29.77) * mm, "end": v(-206.73, -27.77) * mm});
            skLineSegment(sketch, "E107.9.2.2", {"start": v(-206.73, -27.77) * mm, "end": v(-203.26, -29.77) * mm});
            skLineSegment(sketch, "E107.9.2.3", {"start": v(-203.26, -29.77) * mm, "end": v(-203.26, -33.77) * mm});
            skLineSegment(sketch, "E107.9.2.4", {"start": v(-203.26, -33.77) * mm, "end": v(-206.73, -35.77) * mm});
            skLineSegment(sketch, "E107.9.2.5", {"start": v(-206.73, -35.77) * mm, "end": v(-210.2, -33.77) * mm});
            skLineSegment(sketch, "E107.direction1", {"start": v(-210.2, -19.03) * mm, "end": v(-201.2, -19.03) * mm, "construction": true});
            skLineSegment(sketch, "E107.direction2", {"start": v(-210.2, -19.03) * mm, "end": v(-205.94, -26.4) * mm, "construction": true});
            skSolve(sketch);
        }
        {
            var Q0;
            {var subQ16=sQuery(id+"F0.wireOp",EDGE,"E21");Q0=makeQuery(id+"F0.imprint","IMPRINT",FACE,{"disambiguationData":[TD([[makeQuery(id+"F0.imprint","IMPRINT",EDGE,{"derivedFrom":subQ16}),-1.0]])]});}
            var Q1;
            {var subQ0=sQuery(id+"F0.wireOp",EDGE,"E9");Q1=makeQuery(id+"F0.imprint","IMPRINT",FACE,{"disambiguationData":[TD([[makeQuery(id+"F0.imprint","IMPRINT",EDGE,{"derivedFrom":subQ0}),1.0]])]});}
            var Q2;
            {var subQ0=sQuery(id+"F0.wireOp",EDGE,"E12");Q2=makeQuery(id+"F0.imprint","IMPRINT",FACE,{"disambiguationData":[TD([[makeQuery(id+"F0.imprint","IMPRINT",EDGE,{"derivedFrom":subQ0}),1.0]])]});}
            var Q3;
            {var subQ0=sQuery(id+"F0.wireOp",EDGE,"E15");Q3=makeQuery(id+"F0.imprint","IMPRINT",FACE,{"disambiguationData":[TD([[makeQuery(id+"F0.imprint","IMPRINT",EDGE,{"derivedFrom":subQ0}),1.0]])]});}
            var Q4;
            {var subQ0=sQuery(id+"F0.wireOp",EDGE,"E18");Q4=makeQuery(id+"F0.imprint","IMPRINT",FACE,{"disambiguationData":[TD([[makeQuery(id+"F0.imprint","IMPRINT",EDGE,{"derivedFrom":subQ0}),-1.0]])]});}
            var Q5;
            {var subQ0=sQuery(id+"F0.wireOp",EDGE,"E3");Q5=makeQuery(id+"F0.imprint","IMPRINT",FACE,{"disambiguationData":[TD([[makeQuery(id+"F0.imprint","IMPRINT",EDGE,{"derivedFrom":subQ0}),1.0]])]});}
            var Q6;
            {var subQ0=sQuery(id+"F0.wireOp",EDGE,"E6");Q6=makeQuery(id+"F0.imprint","IMPRINT",FACE,{"disambiguationData":[TD([[makeQuery(id+"F0.imprint","IMPRINT",EDGE,{"derivedFrom":subQ0}),1.0]])]});}
            var Q7;
            {var subQ0=sQuery(id+"F0.wireOp",EDGE,"E30");Q7=makeQuery(id+"F0.imprint","IMPRINT",FACE,{"disambiguationData":[TD([[makeQuery(id+"F0.imprint","IMPRINT",EDGE,{"derivedFrom":subQ0}),-1.0]])]});}
            var Q8;
            {var subQ0=sQuery(id+"F0.wireOp",EDGE,"E27");Q8=makeQuery(id+"F0.imprint","IMPRINT",FACE,{"disambiguationData":[TD([[makeQuery(id+"F0.imprint","IMPRINT",EDGE,{"derivedFrom":subQ0}),-1.0]])]});}
            extrude(context, id + "F1", {"entities" : qUnion([Q0, Q1, Q2, Q3, Q4, Q5, Q6, Q7, Q8]), "depth" : 5 * mm, "offsetDistance" : 25 * mm});
        }
        {
            var Q0;
            {var subQ1=sQuery(id+"F0.wireOp",EDGE,"E9");Q0=makeQuery(id+"F0.imprint","IMPRINT",FACE,{"disambiguationData":[TD([[makeQuery(id+"F0.imprint","IMPRINT",EDGE,{"derivedFrom":subQ1}),-1.0]])]});}
            extrude(context, id + "F2", {"entities" : qUnion([Q0]), "depth" : 5 * mm, "offsetDistance" : 25 * mm});
        }
    });
